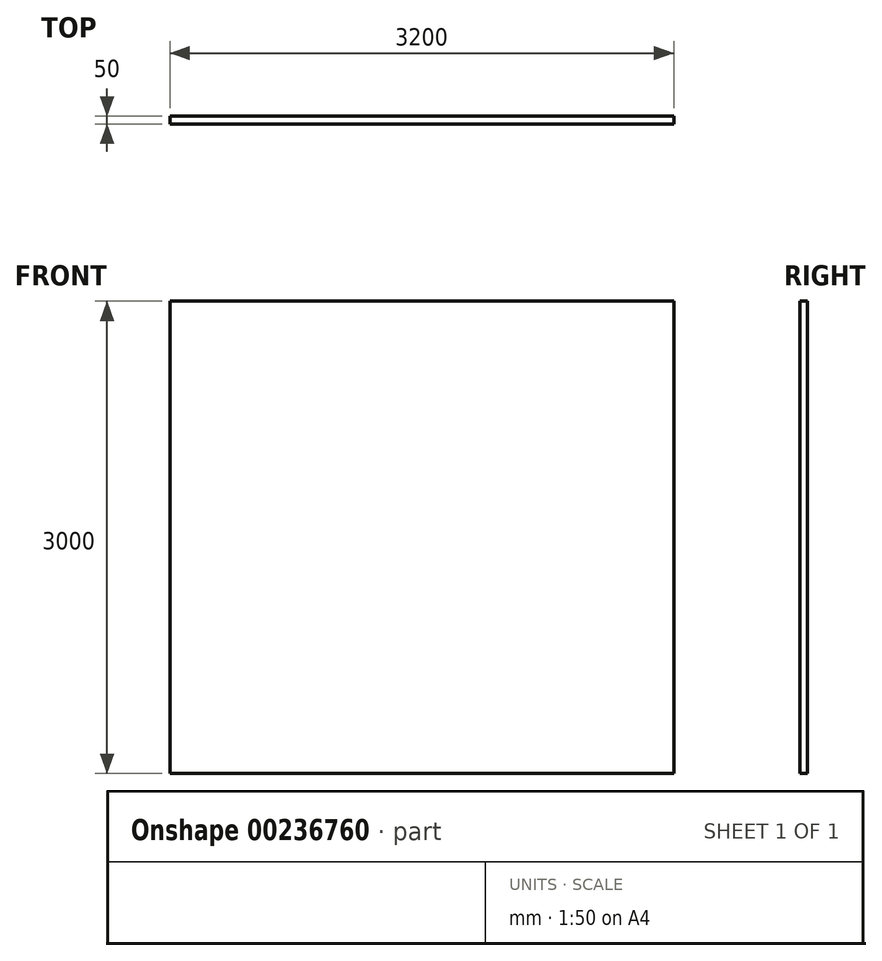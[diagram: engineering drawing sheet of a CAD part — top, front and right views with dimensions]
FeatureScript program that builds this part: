
annotation { "Feature Type Name" : "Feature", "Feature Type Description" : "" }
export const myFeature = defineFeature(function(context is Context, id is Id, definition is map)
    precondition{}
    {
        {
            var Q0;
            Q0=qCreatedBy(makeId("Top.planeOp"),FACE);
            var sketch = newSketch(context, id + "F0", { "sketchPlane" : qUnion([Q0])});
            skLineSegment(sketch, "E0.bottom", {"start": v(-150.6, 0) * mm, "end": v(3049.4, 0) * mm});
            skLineSegment(sketch, "E0.top", {"start": v(-150.6, -50) * mm, "end": v(3049.4, -50) * mm});
            skLineSegment(sketch, "E0.left", {"start": v(-150.6, 0) * mm, "end": v(-150.6, -50) * mm});
            skLineSegment(sketch, "E0.right", {"start": v(3049.4, 0) * mm, "end": v(3049.4, -50) * mm});
            skSolve(sketch);
        }
        {
            var Q0;
            Q0 = qSketchRegion(id + "F0", true);
            extrude(context, id + "F1", {"entities" : qUnion([Q0]), "oppositeDirection" : true, "depth" : 3000 * mm, "offsetDistance" : 25 * mm});
        }
    });
